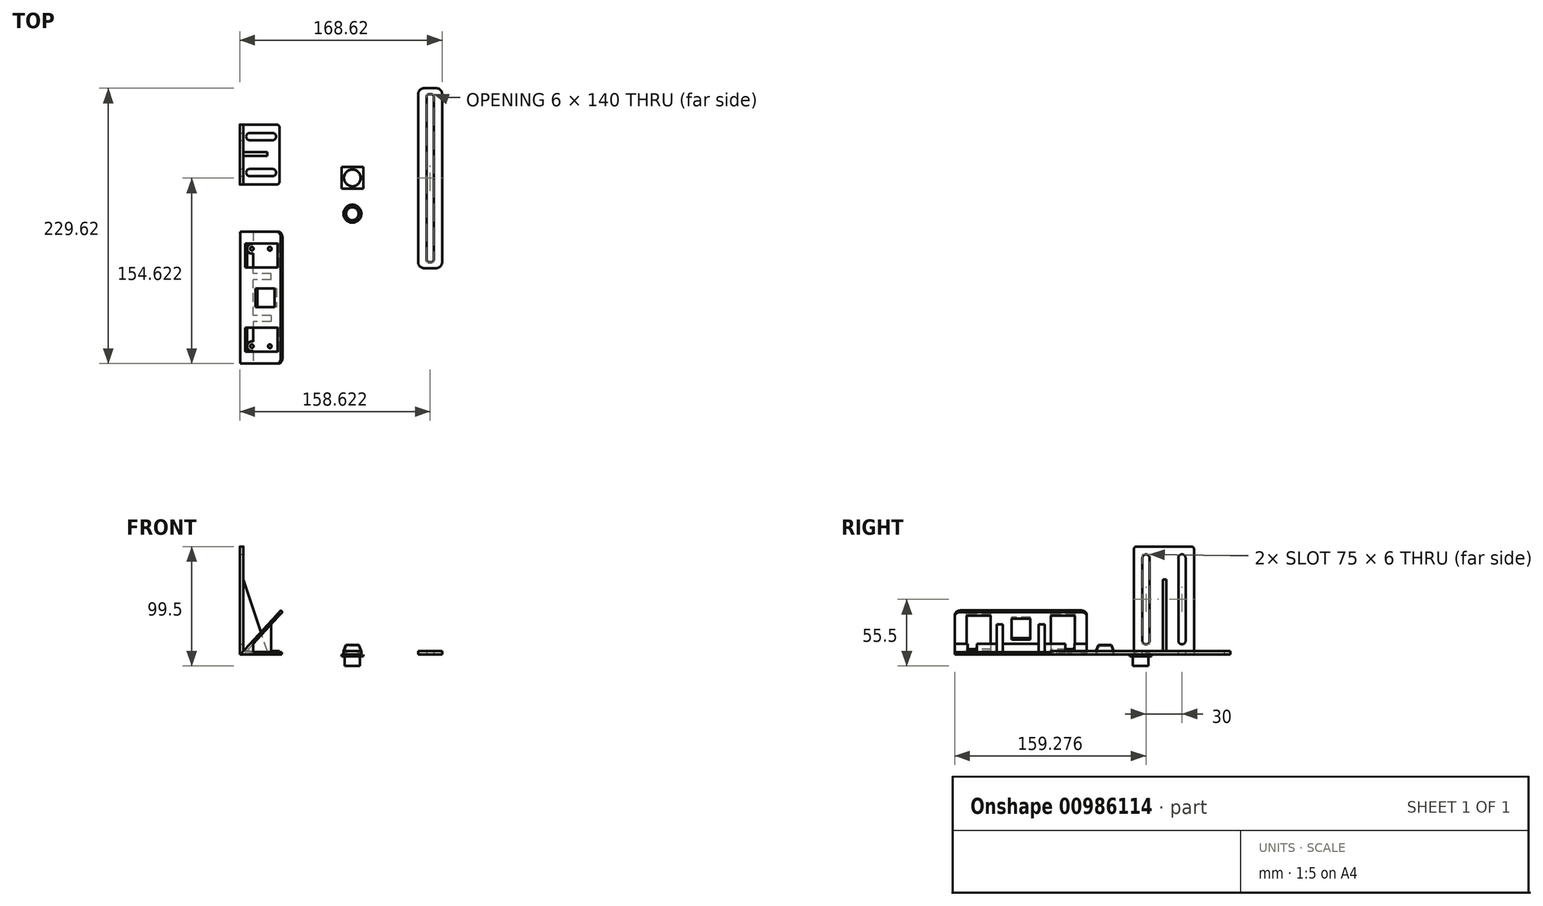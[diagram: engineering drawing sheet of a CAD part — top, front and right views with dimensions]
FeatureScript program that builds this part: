
annotation { "Feature Type Name" : "Feature", "Feature Type Description" : "" }
export const myFeature = defineFeature(function(context is Context, id is Id, definition is map)
    precondition{}
    {
        {
            var Q0;
            Q0=qCreatedBy(makeId("Top.planeOp"),FACE);
            var sketch = newSketch(context, id + "F0", { "sketchPlane" : qUnion([Q0])});
            skCircle(sketch, "E0", {"center": v(0, 0) * mm, "radius": 7 * mm});
            skSolve(sketch);
        }
        {
            var Q0;
            Q0=makeQuery(id+"F0.imprint","IMPRINT",FACE,{"disambiguationData":[TD([[makeQuery(id+"F0.imprint","IMPRINT",EDGE,{"derivedFrom":sQuery(id+"F0.wireOp",EDGE,"E0")}),1.0]])]});
            extrude(context, id + "F1", {"entities" : qUnion([Q0]), "depth" : 2.5 * mm, "offsetDistance" : 25 * mm});
        }
        {
            var Q0;
            Q0=makeQuery(id+"F1.opExtrude","CAP_EDGE",EDGE,{"disambiguationData":[OSD([sQuery(id+"F0.wireOp",EDGE,"E0")])],"isStart":false});
            fillet(context, id + "F2", {"entities" : qUnion([Q0]), "radius" : 7 * mm, "tangentPropagation" : true, "allowEdgeOverflow" : false});
        }
        {
            var Q0;
            Q0=makeQuery(id+"F1.opExtrude","CAP_FACE",FACE,{"disambiguationData":[OSD([sQuery(id+"F0.wireOp",EDGE,"E0")])],"isStart":true});
            cPlane(context, id + "F3", {"entities" : qUnion([Q0]), "cplaneType" : CPlaneType.OFFSET, "offset" : 0 * mm, "width" : 150 * mm, "height" : 150 * mm});
        }
        {
            var Q0;
            Q0=qCreatedBy(id+"F3.planeOp",FACE);
            var sketch = newSketch(context, id + "F4", { "sketchPlane" : qUnion([Q0])});
            skLineSegment(sketch, "E1.bottom", {"start": v(-9, -9) * mm, "end": v(9, -9) * mm});
            skLineSegment(sketch, "E1.top", {"start": v(-9, 9) * mm, "end": v(9, 9) * mm});
            skLineSegment(sketch, "E1.left", {"start": v(-9, -9) * mm, "end": v(-9, 9) * mm});
            skLineSegment(sketch, "E1.right", {"start": v(9, -9) * mm, "end": v(9, 9) * mm});
            skSolve(sketch);
        }
        {
            var Q0;
            Q0=qSketchRegion(id+"F4",true);
            extrude(context, id + "F5", {"entities" : qUnion([Q0]), "operationType" : NewBodyOperationType.ADD, "depth" : 1.5 * mm, "offsetDistance" : 25 * mm});
        }
        {
            var Q0;
            Q0=makeQuery(id+"F5.opExtrude","CAP_FACE",FACE,{"disambiguationData":[OSD([sQuery(id+"F4.wireOp",EDGE,"E1.bottom"),sQuery(id+"F4.wireOp",EDGE,"E1.top"),sQuery(id+"F4.wireOp",EDGE,"E1.left"),sQuery(id+"F4.wireOp",EDGE,"E1.right")])],"isStart":false});
            cPlane(context, id + "F6", {"entities" : qUnion([Q0]), "cplaneType" : CPlaneType.OFFSET, "offset" : 0 * mm, "width" : 150 * mm, "height" : 150 * mm});
        }
        {
            var Q0;
            Q0=qCreatedBy(id+"F6.planeOp",FACE);
            var sketch = newSketch(context, id + "F7", { "sketchPlane" : qUnion([Q0])});
            skCircle(sketch, "E2", {"center": v(0, 0) * mm, "radius": 6.4 * mm});
            skSolve(sketch);
        }
        {
            var Q0;
            Q0=qSketchRegion(id+"F7",true);
            extrude(context, id + "F8", {"entities" : qUnion([Q0]), "operationType" : NewBodyOperationType.ADD, "depth" : 8 * mm, "offsetDistance" : 25 * mm});
        }
        {
            var Q0;
            Q0=qCreatedBy(makeId("Top.planeOp"),FACE);
            var sketch = newSketch(context, id + "F9", { "sketchPlane" : qUnion([Q0])});
            skCircle(sketch, "E3", {"center": v(0, -29.84) * mm, "radius": 7.45 * mm});
            skSolve(sketch);
        }
        {
            var Q0;
            Q0=qSketchRegion(id+"F9",true);
            extrude(context, id + "F10", {"entities" : qUnion([Q0]), "depth" : 8 * mm, "offsetDistance" : 25 * mm});
        }
        {
            var Q0;
            Q0=makeQuery(id+"F10.opExtrude","CAP_EDGE",EDGE,{"disambiguationData":[OSD([sQuery(id+"F9.wireOp",EDGE,"E3")])],"isStart":false});
            chamfer(context, id + "F11", {"entities" : qUnion([Q0]), "chamferType" : ChamferType.TWO_OFFSETS, "width1" : 2 * mm, "oppositeDirection" : false, "width2" : 5 * mm, "tangentPropagation" : true});
        }
        {
            var Q0;
            Q0=qCreatedBy(makeId("Top.planeOp"),FACE);
            var sketch = newSketch(context, id + "F12", { "sketchPlane" : qUnion([Q0])});
            skCircle(sketch, "E4", {"center": v(0, -29.84) * mm, "radius": 6.45 * mm});
            skSolve(sketch);
        }
        {
            var Q0;
            Q0=qSketchRegion(id+"F12",true);
            extrude(context, id + "F13", {"entities" : qUnion([Q0]), "depth" : 7 * mm, "offsetDistance" : 25 * mm});
        }
        {
            var Q0;
            Q0=makeQuery(id+"F13.opExtrude","CAP_EDGE",EDGE,{"disambiguationData":[OSD([sQuery(id+"F12.wireOp",EDGE,"E4")])],"isStart":false});
            chamfer(context, id + "F14", {"entities" : qUnion([Q0]), "chamferType" : ChamferType.TWO_OFFSETS, "width1" : 1.7 * mm, "oppositeDirection" : false, "width2" : 4 * mm, "tangentPropagation" : true});
        }
        {
            var Q0;
            Q0=makeQuery(id+"F13.opExtrude","SWEPT_BODY",BODY,{"disambiguationData":[OSD([sQuery(id+"F12.wireOp",EDGE,"E4")])]});
            var Q1;
            Q1=makeQuery(id+"F10.opExtrude","SWEPT_BODY",BODY,{"disambiguationData":[OSD([sQuery(id+"F9.wireOp",EDGE,"E3")])]});
            booleanBodies(context, id + "F15", {"operationType" : BooleanOperationType.SUBTRACTION, "tools" : qUnion([Q0]), "targets" : qUnion([Q1])});
        }
        {
            var Q0;
            Q0=qCreatedBy(makeId("Top.planeOp"),FACE);
            var sketch = newSketch(context, id + "F16", { "sketchPlane" : qUnion([Q0])});
            skLineSegment(sketch, "E5.bottom", {"start": v(59.8, 74.78) * mm, "end": v(69.8, 74.78) * mm});
            skLineSegment(sketch, "E5.top", {"start": v(59.8, -75.22) * mm, "end": v(69.8, -75.22) * mm});
            skLineSegment(sketch, "E5.left", {"start": v(54.8, 69.78) * mm, "end": v(54.8, -70.22) * mm});
            skLineSegment(sketch, "E5.right", {"start": v(74.8, 69.78) * mm, "end": v(74.8, -70.22) * mm});
            skPoint(sketch, "E6.visualSharp", {"position": v(54.8, 74.78) * mm});
            skArc(sketch, "E6.filletArc", {"start": v(59.8, 74.78) * mm, "mid": v(56.27, 73.32) * mm, "end": v(54.8, 69.78) * mm});
            skPoint(sketch, "E7.visualSharp", {"position": v(74.8, 74.78) * mm});
            skArc(sketch, "E7.filletArc", {"start": v(74.8, 69.78) * mm, "mid": v(73.34, 73.32) * mm, "end": v(69.8, 74.78) * mm});
            skPoint(sketch, "E8.visualSharp", {"position": v(54.8, -75.22) * mm});
            skArc(sketch, "E8.filletArc", {"start": v(54.8, -70.22) * mm, "mid": v(56.27, -73.75) * mm, "end": v(59.8, -75.22) * mm});
            skPoint(sketch, "E9.visualSharp", {"position": v(74.8, -75.22) * mm});
            skArc(sketch, "E9.filletArc", {"start": v(69.8, -75.22) * mm, "mid": v(73.34, -73.75) * mm, "end": v(74.8, -70.22) * mm});
            skLineSegment(sketch, "E10.bottom", {"start": v(63.8, 69.78) * mm, "end": v(65.8, 69.78) * mm});
            skLineSegment(sketch, "E10.top", {"start": v(63.8, -70.22) * mm, "end": v(65.8, -70.22) * mm});
            skLineSegment(sketch, "E10.left", {"start": v(61.8, 67.78) * mm, "end": v(61.8, -68.22) * mm});
            skLineSegment(sketch, "E10.right", {"start": v(67.8, 67.78) * mm, "end": v(67.8, -68.22) * mm});
            skPoint(sketch, "E11.visualSharp", {"position": v(61.8, 69.78) * mm});
            skArc(sketch, "E11.filletArc", {"start": v(63.8, 69.78) * mm, "mid": v(62.39, 69.2) * mm, "end": v(61.8, 67.78) * mm});
            skPoint(sketch, "E12.visualSharp", {"position": v(61.8, -70.22) * mm});
            skArc(sketch, "E12.filletArc", {"start": v(61.8, -68.22) * mm, "mid": v(62.39, -69.63) * mm, "end": v(63.8, -70.22) * mm});
            skPoint(sketch, "E13.visualSharp", {"position": v(67.8, -70.22) * mm});
            skArc(sketch, "E13.filletArc", {"start": v(65.8, -70.22) * mm, "mid": v(67.22, -69.63) * mm, "end": v(67.8, -68.22) * mm});
            skPoint(sketch, "E14.visualSharp", {"position": v(67.8, 69.78) * mm});
            skArc(sketch, "E14.filletArc", {"start": v(67.8, 67.78) * mm, "mid": v(67.22, 69.2) * mm, "end": v(65.8, 69.78) * mm});
            skSolve(sketch);
        }
        {
            var Q0;
            Q0=qSketchRegion(id+"F16",true);
            extrude(context, id + "F17", {"entities" : qUnion([Q0]), "depth" : 3 * mm, "offsetDistance" : 25 * mm});
        }
        {
            var Q0;
            Q0=qCreatedBy(makeId("Top.planeOp"),FACE);
            var sketch = newSketch(context, id + "F18", { "sketchPlane" : qUnion([Q0])});
            skLineSegment(sketch, "E15.bottom", {"start": v(-90.82, 44.44) * mm, "end": v(-62.82, 44.44) * mm});
            skLineSegment(sketch, "E15.top", {"start": v(-90.82, -5.56) * mm, "end": v(-62.82, -5.56) * mm});
            skLineSegment(sketch, "E15.left", {"start": v(-90.82, 44.44) * mm, "end": v(-90.82, -5.56) * mm});
            skLineSegment(sketch, "E15.right", {"start": v(-60.82, 42.44) * mm, "end": v(-60.82, -3.56) * mm});
            skPoint(sketch, "E16.visualSharp", {"position": v(-60.82, 44.44) * mm});
            skArc(sketch, "E16.filletArc", {"start": v(-60.82, 42.44) * mm, "mid": v(-61.4, 43.85) * mm, "end": v(-62.82, 44.44) * mm});
            skPoint(sketch, "E17.visualSharp", {"position": v(-60.82, -5.56) * mm});
            skArc(sketch, "E17.filletArc", {"start": v(-62.82, -5.56) * mm, "mid": v(-61.4, -4.98) * mm, "end": v(-60.82, -3.56) * mm});
            skLineSegment(sketch, "E18.bottom", {"start": v(-101.44, 55.6) * mm, "end": v(-90.82, 55.6) * mm, "construction": true});
            skLineSegment(sketch, "E18.top", {"start": v(-101.44, -19.09) * mm, "end": v(-90.82, -19.09) * mm, "construction": true});
            skLineSegment(sketch, "E18.left", {"start": v(-101.44, 55.6) * mm, "end": v(-101.44, -19.09) * mm, "construction": true});
            skLineSegment(sketch, "E18.right", {"start": v(-90.82, 55.6) * mm, "end": v(-90.82, -19.09) * mm, "construction": true});
            skSolve(sketch);
        }
        {
            var Q0;
            Q0=qSketchRegion(id+"F18",true);
            extrude(context, id + "F19", {"entities" : qUnion([Q0]), "depth" : 3 * mm, "offsetDistance" : 25 * mm});
        }
        {
            var Q0;
            Q0=qCreatedBy(makeId("Top.planeOp"),FACE);
            var sketch = newSketch(context, id + "F20", { "sketchPlane" : qUnion([Q0])});
            skLineSegment(sketch, "E19.bottom", {"start": v(-93.82, 44.44) * mm, "end": v(-90.82, 44.44) * mm});
            skLineSegment(sketch, "E19.top", {"start": v(-93.82, -5.56) * mm, "end": v(-90.82, -5.56) * mm});
            skLineSegment(sketch, "E19.left", {"start": v(-93.82, 44.44) * mm, "end": v(-93.82, -5.56) * mm});
            skLineSegment(sketch, "E19.right", {"start": v(-90.82, 44.44) * mm, "end": v(-90.82, -5.56) * mm});
            skSolve(sketch);
        }
        {
            var Q0;
            Q0=qSketchRegion(id+"F20",true);
            extrude(context, id + "F21", {"entities" : qUnion([Q0]), "operationType" : NewBodyOperationType.ADD, "depth" : 90 * mm, "offsetDistance" : 25 * mm});
        }
        {
            var Q0;
            Q0=makeQuery(id+"F21.opExtrude","CAP_EDGE",EDGE,{"disambiguationData":[OSD([sQuery(id+"F20.wireOp",EDGE,"E19.top")])],"isStart":false});
            var Q1;
            Q1=makeQuery(id+"F21.opExtrude","CAP_EDGE",EDGE,{"disambiguationData":[OSD([sQuery(id+"F20.wireOp",EDGE,"E19.bottom")])],"isStart":false});
            fillet(context, id + "F22", {"entities" : qUnion([Q0, Q1]), "radius" : 2 * mm, "tangentPropagation" : true, "allowEdgeOverflow" : false});
        }
        {
            var Q0;
            Q0=makeQuery(id+"F19.opExtrude","CAP_FACE",FACE,{"disambiguationData":[OSD([sQuery(id+"F18.wireOp",EDGE,"E15.bottom"),sQuery(id+"F18.wireOp",EDGE,"E15.top"),sQuery(id+"F18.wireOp",EDGE,"E15.left"),sQuery(id+"F18.wireOp",EDGE,"E15.right"),sQuery(id+"F18.wireOp",EDGE,"E16.filletArc"),sQuery(id+"F18.wireOp",EDGE,"E17.filletArc")])],"isStart":false});
            var sketch = newSketch(context, id + "F23", { "sketchPlane" : qUnion([Q0])});
            skLineSegment(sketch, "E20.bottom", {"start": v(-85.49, 37.44) * mm, "end": v(-66.49, 37.44) * mm});
            skLineSegment(sketch, "E20.top", {"start": v(-85.49, 31.44) * mm, "end": v(-66.49, 31.44) * mm});
            skLineSegment(sketch, "E20.left", {"start": v(-88.49, 34.44) * mm, "end": v(-88.49, 34.44) * mm});
            skLineSegment(sketch, "E20.right", {"start": v(-63.49, 34.44) * mm, "end": v(-63.49, 34.44) * mm});
            skPoint(sketch, "E21.visualSharp", {"position": v(-88.49, 37.44) * mm});
            skArc(sketch, "E21.filletArc", {"start": v(-85.49, 37.44) * mm, "mid": v(-87.6, 36.56) * mm, "end": v(-88.49, 34.44) * mm});
            skPoint(sketch, "E22.visualSharp", {"position": v(-88.49, 31.44) * mm});
            skArc(sketch, "E22.filletArc", {"start": v(-88.49, 34.44) * mm, "mid": v(-87.6, 32.31) * mm, "end": v(-85.49, 31.44) * mm});
            skPoint(sketch, "E23.visualSharp", {"position": v(-63.49, 31.44) * mm});
            skArc(sketch, "E23.filletArc", {"start": v(-66.49, 31.44) * mm, "mid": v(-64.37, 32.31) * mm, "end": v(-63.49, 34.44) * mm});
            skPoint(sketch, "E24.visualSharp", {"position": v(-63.49, 37.44) * mm});
            skArc(sketch, "E24.filletArc", {"start": v(-63.49, 34.44) * mm, "mid": v(-64.37, 36.56) * mm, "end": v(-66.49, 37.44) * mm});
            skLineSegment(sketch, "E25.bottom", {"start": v(-85.49, 7.44) * mm, "end": v(-66.49, 7.44) * mm});
            skLineSegment(sketch, "E25.top", {"start": v(-85.49, 1.44) * mm, "end": v(-66.49, 1.44) * mm});
            skLineSegment(sketch, "E25.left", {"start": v(-88.49, 4.44) * mm, "end": v(-88.49, 4.44) * mm});
            skLineSegment(sketch, "E25.right", {"start": v(-63.49, 4.44) * mm, "end": v(-63.49, 4.44) * mm});
            skPoint(sketch, "E26.visualSharp", {"position": v(-88.49, 7.44) * mm});
            skArc(sketch, "E26.filletArc", {"start": v(-85.49, 7.44) * mm, "mid": v(-87.61, 6.56) * mm, "end": v(-88.49, 4.44) * mm});
            skPoint(sketch, "E27.visualSharp", {"position": v(-88.49, 1.44) * mm});
            skArc(sketch, "E27.filletArc", {"start": v(-88.49, 4.44) * mm, "mid": v(-87.61, 2.31) * mm, "end": v(-85.49, 1.44) * mm});
            skPoint(sketch, "E28.visualSharp", {"position": v(-63.49, 1.44) * mm});
            skArc(sketch, "E28.filletArc", {"start": v(-66.49, 1.44) * mm, "mid": v(-64.37, 2.31) * mm, "end": v(-63.49, 4.44) * mm});
            skPoint(sketch, "E29.visualSharp", {"position": v(-63.49, 7.44) * mm});
            skArc(sketch, "E29.filletArc", {"start": v(-63.49, 4.44) * mm, "mid": v(-64.37, 6.56) * mm, "end": v(-66.49, 7.44) * mm});
            skSolve(sketch);
        }
        {
            var Q0;
            Q0=qSketchRegion(id+"F23",true);
            extrude(context, id + "F24", {"entities" : qUnion([Q0]), "operationType" : NewBodyOperationType.REMOVE, "oppositeDirection" : true, "depth" : 25 * mm, "offsetDistance" : 25 * mm});
        }
        {
            var Q0;
            Q0=makeQuery(id+"F21.opExtrude","SWEPT_FACE",FACE,{"disambiguationData":[OSD([sQuery(id+"F20.wireOp",EDGE,"E19.right")])]});
            var sketch = newSketch(context, id + "F25", { "sketchPlane" : qUnion([Q0])});
            skLineSegment(sketch, "E30.bottom", {"start": v(34.44, 83.5) * mm, "end": v(34.44, 83.5) * mm});
            skLineSegment(sketch, "E30.top", {"start": v(34.44, 8.5) * mm, "end": v(34.44, 8.5) * mm});
            skLineSegment(sketch, "E30.left", {"start": v(31.44, 80.5) * mm, "end": v(31.44, 11.5) * mm});
            skLineSegment(sketch, "E30.right", {"start": v(37.44, 80.5) * mm, "end": v(37.44, 11.5) * mm});
            skPoint(sketch, "E31.visualSharp", {"position": v(31.44, 83.5) * mm});
            skArc(sketch, "E31.filletArc", {"start": v(34.44, 83.5) * mm, "mid": v(32.31, 82.62) * mm, "end": v(31.44, 80.5) * mm});
            skPoint(sketch, "E32.visualSharp", {"position": v(31.44, 8.5) * mm});
            skArc(sketch, "E32.filletArc", {"start": v(31.44, 11.5) * mm, "mid": v(32.31, 9.38) * mm, "end": v(34.44, 8.5) * mm});
            skPoint(sketch, "E33.visualSharp", {"position": v(37.44, 83.5) * mm});
            skArc(sketch, "E33.filletArc", {"start": v(37.44, 80.5) * mm, "mid": v(36.56, 82.62) * mm, "end": v(34.44, 83.5) * mm});
            skPoint(sketch, "E34.visualSharp", {"position": v(37.44, 8.5) * mm});
            skArc(sketch, "E34.filletArc", {"start": v(34.44, 8.5) * mm, "mid": v(36.56, 9.38) * mm, "end": v(37.44, 11.5) * mm});
            skLineSegment(sketch, "E35.bottom", {"start": v(49.07, 61.34) * mm, "end": v(49.07, 61.34) * mm});
            skLineSegment(sketch, "E35.top", {"start": v(49.07, -13.66) * mm, "end": v(49.07, -13.66) * mm});
            skLineSegment(sketch, "E35.left", {"start": v(1.44, 80.5) * mm, "end": v(1.44, 11.5) * mm});
            skLineSegment(sketch, "E35.right", {"start": v(7.44, 80.5) * mm, "end": v(7.44, 11.5) * mm});
            skPoint(sketch, "E36.visualSharp", {"position": v(1.44, 83.5) * mm});
            skArc(sketch, "E36.filletArc", {"start": v(4.44, 83.5) * mm, "mid": v(2.31, 82.62) * mm, "end": v(1.44, 80.5) * mm});
            skPoint(sketch, "E37.visualSharp", {"position": v(1.44, 8.5) * mm});
            skArc(sketch, "E37.filletArc", {"start": v(1.44, 11.5) * mm, "mid": v(2.31, 9.38) * mm, "end": v(4.44, 8.5) * mm});
            skPoint(sketch, "E38.visualSharp", {"position": v(7.44, 83.5) * mm});
            skArc(sketch, "E38.filletArc", {"start": v(7.44, 80.5) * mm, "mid": v(6.56, 82.62) * mm, "end": v(4.44, 83.5) * mm});
            skPoint(sketch, "E39.visualSharp", {"position": v(7.44, 8.5) * mm});
            skArc(sketch, "E39.filletArc", {"start": v(4.44, 8.5) * mm, "mid": v(6.56, 9.38) * mm, "end": v(7.44, 11.5) * mm});
            skSolve(sketch);
        }
        {
            var Q0;
            Q0=qSketchRegion(id+"F25",true);
            extrude(context, id + "F26", {"entities" : qUnion([Q0]), "operationType" : NewBodyOperationType.REMOVE, "oppositeDirection" : true, "depth" : 25 * mm, "offsetDistance" : 25 * mm});
        }
        {
            var Q0;
            Q0=makeQuery(id+"F29.boolean.opBoolean","MERGE",FACE,{"derivedFrom":[makeQuery(id+"F21.boolean.opBoolean","MERGE",FACE,{"derivedFrom":[makeQuery(id+"F19.opExtrude","SWEPT_FACE",FACE,{"disambiguationData":[OSD([sQuery(id+"F18.wireOp",EDGE,"E15.top")])]}),makeQuery(id+"F21.opExtrude","SWEPT_FACE",FACE,{"disambiguationData":[OSD([sQuery(id+"F20.wireOp",EDGE,"E19.top")])]})]}),makeQuery(id+"F29.opExtrude","CAP_FACE",FACE,{"disambiguationData":[OSD([sQuery(id+"F28.wireOp",EDGE,"E40"),sQuery(id+"F28.wireOp",EDGE,"E41"),sQuery(id+"F28.wireOp",EDGE,"E42")])],"isStart":true})]});
            cPlane(context, id + "F27", {"entities" : qUnion([Q0]), "cplaneType" : CPlaneType.OFFSET, "offset" : 24 * mm, "oppositeDirection" : true, "width" : 150 * mm, "height" : 150 * mm});
        }
        {
            var Q0;
            Q0=qCreatedBy(id+"F27.planeOp",FACE);
            var sketch = newSketch(context, id + "F28", { "sketchPlane" : qUnion([Q0])});
            skLineSegment(sketch, "E40", {"start": v(-90.82, 62.64) * mm, "end": v(-90.82, 3) * mm});
            skLineSegment(sketch, "E41", {"start": v(-90.82, 3) * mm, "end": v(-70.95, 3) * mm});
            skLineSegment(sketch, "E42", {"start": v(-70.95, 3) * mm, "end": v(-90.82, 62.64) * mm});
            skSolve(sketch);
        }
        {
            var Q0;
            Q0=makeQuery(id+"F28.imprint","IMPRINT",FACE,{"disambiguationData":[TD([[makeQuery(id+"F28.imprint","IMPRINT",EDGE,{"derivedFrom":sQuery(id+"F28.wireOp",EDGE,"E40")}),1.0]])]});
            extrude(context, id + "F29", {"entities" : qUnion([Q0]), "operationType" : NewBodyOperationType.ADD, "oppositeDirection" : true, "depth" : 3 * mm, "offsetDistance" : 25 * mm});
        }
        {
            var Q0;
            Q0=qCreatedBy(makeId("Top.planeOp"),FACE);
            var sketch = newSketch(context, id + "F30", { "sketchPlane" : qUnion([Q0])});
            skLineSegment(sketch, "E43.bottom", {"start": v(-88.77, -44.84) * mm, "end": v(-63.77, -44.84) * mm});
            skLineSegment(sketch, "E43.top", {"start": v(-88.77, -154.84) * mm, "end": v(-63.77, -154.84) * mm});
            skLineSegment(sketch, "E43.left", {"start": v(-88.77, -44.84) * mm, "end": v(-88.77, -154.84) * mm});
            skLineSegment(sketch, "E43.right", {"start": v(-58.77, -49.84) * mm, "end": v(-58.77, -149.84) * mm});
            skPoint(sketch, "E44.visualSharp", {"position": v(-58.77, -44.84) * mm});
            skArc(sketch, "E44.filletArc", {"start": v(-58.77, -49.84) * mm, "mid": v(-60.23, -46.3) * mm, "end": v(-63.77, -44.84) * mm});
            skPoint(sketch, "E45.visualSharp", {"position": v(-58.77, -154.84) * mm});
            skArc(sketch, "E45.filletArc", {"start": v(-63.77, -154.84) * mm, "mid": v(-60.23, -153.38) * mm, "end": v(-58.77, -149.84) * mm});
            skSolve(sketch);
        }
        {
            var Q0;
            Q0=qSketchRegion(id+"F30",true);
            extrude(context, id + "F31", {"entities" : qUnion([Q0]), "depth" : 2 * mm, "offsetDistance" : 25 * mm});
        }
        {
            var Q0;
            Q0=makeQuery(id+"F31.opExtrude","SWEPT_FACE",FACE,{"disambiguationData":[OSD([sQuery(id+"F30.wireOp",EDGE,"E43.top")])]});
            var sketch = newSketch(context, id + "F32", { "sketchPlane" : qUnion([Q0])});
            skLineSegment(sketch, "E46", {"start": v(-88.77, 2) * mm, "end": v(-58.2, 35.45) * mm});
            skLineSegment(sketch, "E47", {"start": v(-58.2, 35.45) * mm, "end": v(-59.67, 36.8) * mm});
            skLineSegment(sketch, "E48", {"start": v(-59.67, 36.8) * mm, "end": v(-93.3, 0) * mm});
            skLineSegment(sketch, "E49", {"start": v(-93.3, 0) * mm, "end": v(-88.77, 0) * mm});
            skLineSegment(sketch, "E50", {"start": v(-88.77, 0) * mm, "end": v(-88.77, 2) * mm});
            skSolve(sketch);
        }
        {
            var Q0;
            Q0=qSketchRegion(id+"F32",true);
            extrude(context, id + "F33", {"entities" : qUnion([Q0]), "operationType" : NewBodyOperationType.ADD, "oppositeDirection" : true, "depth" : 110 * mm, "offsetDistance" : 25 * mm});
        }
        {
            var Q0;
            Q0=makeQuery(id+"F33.opExtrude","CAP_EDGE",EDGE,{"disambiguationData":[OSD([sQuery(id+"F32.wireOp",EDGE,"E47")])],"isStart":true});
            var Q1;
            Q1=makeQuery(id+"F33.opExtrude","CAP_EDGE",EDGE,{"disambiguationData":[OSD([sQuery(id+"F32.wireOp",EDGE,"E47")])],"isStart":false});
            fillet(context, id + "F34", {"entities" : qUnion([Q0, Q1]), "radius" : 5 * mm, "tangentPropagation" : true, "allowEdgeOverflow" : false});
        }
        {
            var Q0;
            Q0=makeQuery(id+"F33.boolean.opBoolean","MERGE",FACE,{"derivedFrom":[makeQuery(id+"F31.opExtrude","SWEPT_FACE",FACE,{"disambiguationData":[OSD([sQuery(id+"F30.wireOp",EDGE,"E43.top")])]}),makeQuery(id+"F33.opExtrude","CAP_FACE",FACE,{"disambiguationData":[OSD([sQuery(id+"F32.wireOp",EDGE,"E46"),sQuery(id+"F32.wireOp",EDGE,"E47"),sQuery(id+"F32.wireOp",EDGE,"E48"),sQuery(id+"F32.wireOp",EDGE,"E49"),sQuery(id+"F32.wireOp",EDGE,"E50")])],"isStart":true})]});
            var sketch = newSketch(context, id + "F35", { "sketchPlane" : qUnion([Q0])});
            skLineSegment(sketch, "E51", {"start": v(-88.77, 2) * mm, "end": v(-82.5, 8.86) * mm});
            skLineSegment(sketch, "E52", {"start": v(-82.5, 8.86) * mm, "end": v(-82.5, 2) * mm});
            skLineSegment(sketch, "E53", {"start": v(-82.5, 2) * mm, "end": v(-88.77, 2) * mm});
            skSolve(sketch);
        }
        {
            var Q0;
            Q0=qSketchRegion(id+"F35",true);
            extrude(context, id + "F36", {"entities" : qUnion([Q0]), "operationType" : NewBodyOperationType.ADD, "oppositeDirection" : true, "depth" : 110 * mm, "offsetDistance" : 25 * mm});
        }
        {
            var Q0;
            Q0=qCreatedBy(makeId("Top.planeOp"),FACE);
            cPlane(context, id + "F37", {"entities" : qUnion([Q0]), "cplaneType" : CPlaneType.OFFSET, "offset" : 50 * mm, "width" : 150 * mm, "height" : 150 * mm});
        }
        {
            var Q0;
            Q0=qCreatedBy(id+"F37.planeOp",FACE);
            var sketch = newSketch(context, id + "F38", { "sketchPlane" : qUnion([Q0])});
            skPoint(sketch, "E54", {"position": v(-68.77, -59.07) * mm});
            skPoint(sketch, "E55", {"position": v(-83.77, -59.07) * mm});
            skPoint(sketch, "E56", {"position": v(-68.77, -140.34) * mm});
            skPoint(sketch, "E57", {"position": v(-83.77, -140.34) * mm});
            skSolve(sketch);
        }
        {
            var Q0;
            Q0=sQuery(id+"F38.wireOp",VERTEX,"E57");
            var Q1;
            Q1=sQuery(id+"F38.wireOp",VERTEX,"E56");
            var Q2;
            Q2=sQuery(id+"F38.wireOp",VERTEX,"E55");
            var Q3;
            Q3=sQuery(id+"F38.wireOp",VERTEX,"E54");
            var Q4;
            Q4=makeQuery(id+"F31.opExtrude","SWEPT_BODY",BODY,{"disambiguationData":[OSD([sQuery(id+"F30.wireOp",EDGE,"E43.bottom"),sQuery(id+"F30.wireOp",EDGE,"E43.top"),sQuery(id+"F30.wireOp",EDGE,"E43.left"),sQuery(id+"F30.wireOp",EDGE,"E43.right"),sQuery(id+"F30.wireOp",EDGE,"E44.filletArc"),sQuery(id+"F30.wireOp",EDGE,"E45.filletArc")])]});
            hole(context, id + "F39", {"style" : HoleStyle.SIMPLE, "endStyle" : HoleEndStyle.BLIND, "holeDiameter" : 3 * mm, "holeDepth" : 50 * mm, "tappedDepth" : 12 * mm, "tapClearance" : 3, "locations" : qUnion([Q0, Q1, Q2, Q3]), "scope" : qUnion([Q4])});
        }
        {
            var Q0;
            Q0=qCreatedBy(id+"F37.planeOp",FACE);
            var sketch = newSketch(context, id + "F40", { "sketchPlane" : qUnion([Q0])});
            skPoint(sketch, "E58", {"position": v(-68.77, -59.07) * mm});
            skPoint(sketch, "E59", {"position": v(-83.77, -59.07) * mm});
            skPoint(sketch, "E60", {"position": v(-68.77, -140.34) * mm});
            skPoint(sketch, "E61", {"position": v(-83.77, -140.34) * mm});
            skSolve(sketch);
        }
        {
            var Q0;
            Q0=sQuery(id+"F40.wireOp",VERTEX,"E61");
            var Q1;
            Q1=sQuery(id+"F40.wireOp",VERTEX,"E60");
            var Q2;
            Q2=sQuery(id+"F40.wireOp",VERTEX,"E58");
            var Q3;
            Q3=sQuery(id+"F40.wireOp",VERTEX,"E59");
            var Q4;
            Q4=makeQuery(id+"F31.opExtrude","SWEPT_BODY",BODY,{"disambiguationData":[OSD([sQuery(id+"F30.wireOp",EDGE,"E43.bottom"),sQuery(id+"F30.wireOp",EDGE,"E43.top"),sQuery(id+"F30.wireOp",EDGE,"E43.left"),sQuery(id+"F30.wireOp",EDGE,"E43.right"),sQuery(id+"F30.wireOp",EDGE,"E44.filletArc"),sQuery(id+"F30.wireOp",EDGE,"E45.filletArc")])]});
            hole(context, id + "F41", {"style" : HoleStyle.SIMPLE, "endStyle" : HoleEndStyle.BLIND, "holeDiameter" : 8 * mm, "holeDepth" : 19 * mm, "tappedDepth" : 12 * mm, "tapClearance" : 3, "locations" : qUnion([Q0, Q1, Q2, Q3]), "scope" : qUnion([Q4])});
        }
        {
            var Q0;
            Q0=makeQuery(id+"F33.boolean.opBoolean","MERGE",FACE,{"derivedFrom":[makeQuery(id+"F31.opExtrude","CAP_FACE",FACE,{"disambiguationData":[OSD([sQuery(id+"F30.wireOp",EDGE,"E43.bottom"),sQuery(id+"F30.wireOp",EDGE,"E43.top"),sQuery(id+"F30.wireOp",EDGE,"E43.left"),sQuery(id+"F30.wireOp",EDGE,"E43.right"),sQuery(id+"F30.wireOp",EDGE,"E44.filletArc"),sQuery(id+"F30.wireOp",EDGE,"E45.filletArc")])],"isStart":true}),makeQuery(id+"F33.opExtrude","SWEPT_FACE",FACE,{"disambiguationData":[OSD([sQuery(id+"F32.wireOp",EDGE,"E49")])]})]});
            var sketch = newSketch(context, id + "F42", { "sketchPlane" : qUnion([Q0])});
            skCircle(sketch, "E62", {"center": v(-83.77, 59.07) * mm, "radius": 4 * mm});
            skCircle(sketch, "E63", {"center": v(-83.77, 140.34) * mm, "radius": 4 * mm});
            skSolve(sketch);
        }
        {
            var Q0;
            Q0=qSketchRegion(id+"F42",true);
            extrude(context, id + "F43", {"entities" : qUnion([Q0]), "operationType" : NewBodyOperationType.ADD, "oppositeDirection" : true, "depth" : 2 * mm, "offsetDistance" : 25 * mm});
        }
        {
            var Q0;
            Q0=makeQuery(id+"F43.boolean.opBoolean","MERGE",FACE,{"derivedFrom":[makeQuery(id+"F31.opExtrude","CAP_FACE",FACE,{"disambiguationData":[OSD([sQuery(id+"F30.wireOp",EDGE,"E43.bottom"),sQuery(id+"F30.wireOp",EDGE,"E43.top"),sQuery(id+"F30.wireOp",EDGE,"E43.left"),sQuery(id+"F30.wireOp",EDGE,"E43.right"),sQuery(id+"F30.wireOp",EDGE,"E44.filletArc"),sQuery(id+"F30.wireOp",EDGE,"E45.filletArc")])],"isStart":false}),makeQuery(id+"F43.opExtrude","CAP_FACE",FACE,{"disambiguationData":[OSD([sQuery(id+"F42.wireOp",EDGE,"E62")])],"isStart":false}),makeQuery(id+"F43.opExtrude","CAP_FACE",FACE,{"disambiguationData":[OSD([sQuery(id+"F42.wireOp",EDGE,"E63")])],"isStart":false})]});
            var sketch = newSketch(context, id + "F44", { "sketchPlane" : qUnion([Q0])});
            skPoint(sketch, "E64", {"position": v(-83.77, -59.07) * mm});
            skPoint(sketch, "E65", {"position": v(-83.77, -140.34) * mm});
            skSolve(sketch);
        }
        {
            var Q0;
            Q0=sQuery(id+"F44.wireOp",VERTEX,"E64");
            var Q1;
            Q1=sQuery(id+"F44.wireOp",VERTEX,"E65");
            var Q2;
            Q2=makeQuery(id+"F31.opExtrude","SWEPT_BODY",BODY,{"disambiguationData":[OSD([sQuery(id+"F30.wireOp",EDGE,"E43.bottom"),sQuery(id+"F30.wireOp",EDGE,"E43.top"),sQuery(id+"F30.wireOp",EDGE,"E43.left"),sQuery(id+"F30.wireOp",EDGE,"E43.right"),sQuery(id+"F30.wireOp",EDGE,"E44.filletArc"),sQuery(id+"F30.wireOp",EDGE,"E45.filletArc")])]});
            hole(context, id + "F45", {"style" : HoleStyle.SIMPLE, "endStyle" : HoleEndStyle.BLIND, "holeDiameter" : 3 * mm, "holeDepth" : 19 * mm, "tappedDepth" : 12 * mm, "tapClearance" : 3, "locations" : qUnion([Q0, Q1]), "scope" : qUnion([Q2])});
        }
        {
            var Q0;
            Q0=makeQuery(id+"F33.opExtrude","SWEPT_FACE",FACE,{"disambiguationData":[OSD([sQuery(id+"F32.wireOp",EDGE,"E48")])]});
            cPlane(context, id + "F46", {"entities" : qUnion([Q0]), "cplaneType" : CPlaneType.OFFSET, "offset" : 25 * mm, "width" : 150 * mm, "height" : 150 * mm});
        }
        {
            var Q0;
            Q0=qCreatedBy(id+"F46.planeOp",FACE);
            var sketch = newSketch(context, id + "F47", { "sketchPlane" : qUnion([Q0])});
            skLineSegment(sketch, "E66.bottom", {"start": v(54.84, -16.95) * mm, "end": v(74.84, -16.95) * mm});
            skLineSegment(sketch, "E66.top", {"start": v(54.84, -56.95) * mm, "end": v(74.84, -56.95) * mm});
            skLineSegment(sketch, "E66.left", {"start": v(54.84, -16.95) * mm, "end": v(54.84, -56.95) * mm});
            skLineSegment(sketch, "E66.right", {"start": v(74.84, -16.95) * mm, "end": v(74.84, -56.95) * mm});
            skLineSegment(sketch, "E67.bottom", {"start": v(124.84, -16.95) * mm, "end": v(144.84, -16.95) * mm});
            skLineSegment(sketch, "E67.top", {"start": v(124.84, -56.95) * mm, "end": v(144.84, -56.95) * mm});
            skLineSegment(sketch, "E67.left", {"start": v(124.84, -16.95) * mm, "end": v(124.84, -56.95) * mm});
            skLineSegment(sketch, "E67.right", {"start": v(144.84, -16.95) * mm, "end": v(144.84, -56.95) * mm});
            skLineSegment(sketch, "E68.bottom", {"start": v(92.04, -20.68) * mm, "end": v(107.66, -20.68) * mm});
            skLineSegment(sketch, "E68.top", {"start": v(92.04, -44.21) * mm, "end": v(107.66, -44.21) * mm});
            skLineSegment(sketch, "E68.left", {"start": v(92.04, -20.68) * mm, "end": v(92.04, -44.21) * mm});
            skLineSegment(sketch, "E68.right", {"start": v(107.66, -20.68) * mm, "end": v(107.66, -44.21) * mm});
            skSolve(sketch);
        }
        {
            var Q0;
            Q0=qSketchRegion(id+"F47",true);
            extrude(context, id + "F48", {"entities" : qUnion([Q0]), "operationType" : NewBodyOperationType.REMOVE, "oppositeDirection" : true, "depth" : 27 * mm, "offsetDistance" : 25 * mm});
        }
        {
            var Q0;
            Q0=makeQuery(id+"F36.boolean.opBoolean","MERGE",FACE,{"derivedFrom":[makeQuery(id+"F33.boolean.opBoolean","MERGE",FACE,{"derivedFrom":[makeQuery(id+"F31.opExtrude","SWEPT_FACE",FACE,{"disambiguationData":[OSD([sQuery(id+"F30.wireOp",EDGE,"E43.top")])]}),makeQuery(id+"F33.opExtrude","CAP_FACE",FACE,{"disambiguationData":[OSD([sQuery(id+"F32.wireOp",EDGE,"E46"),sQuery(id+"F32.wireOp",EDGE,"E47"),sQuery(id+"F32.wireOp",EDGE,"E48"),sQuery(id+"F32.wireOp",EDGE,"E49"),sQuery(id+"F32.wireOp",EDGE,"E50")])],"isStart":true})]}),makeQuery(id+"F36.opExtrude","CAP_FACE",FACE,{"disambiguationData":[OSD([sQuery(id+"F35.wireOp",EDGE,"E51"),sQuery(id+"F35.wireOp",EDGE,"E52"),sQuery(id+"F35.wireOp",EDGE,"E53")])],"isStart":true})]});
            cPlane(context, id + "F49", {"entities" : qUnion([Q0]), "cplaneType" : CPlaneType.OFFSET, "offset" : 35 * mm, "oppositeDirection" : true, "width" : 150 * mm, "height" : 150 * mm});
        }
        {
            var Q0;
            Q0=makeQuery(id+"F36.boolean.opBoolean","MERGE",FACE,{"derivedFrom":[makeQuery(id+"F33.boolean.opBoolean","MERGE",FACE,{"derivedFrom":[makeQuery(id+"F31.opExtrude","SWEPT_FACE",FACE,{"disambiguationData":[OSD([sQuery(id+"F30.wireOp",EDGE,"E43.bottom")])]}),makeQuery(id+"F33.opExtrude","CAP_FACE",FACE,{"disambiguationData":[OSD([sQuery(id+"F32.wireOp",EDGE,"E46"),sQuery(id+"F32.wireOp",EDGE,"E47"),sQuery(id+"F32.wireOp",EDGE,"E48"),sQuery(id+"F32.wireOp",EDGE,"E49"),sQuery(id+"F32.wireOp",EDGE,"E50")])],"isStart":false})]}),makeQuery(id+"F36.opExtrude","CAP_FACE",FACE,{"disambiguationData":[OSD([sQuery(id+"F35.wireOp",EDGE,"E51"),sQuery(id+"F35.wireOp",EDGE,"E52"),sQuery(id+"F35.wireOp",EDGE,"E53")])],"isStart":false})]});
            cPlane(context, id + "F50", {"entities" : qUnion([Q0]), "cplaneType" : CPlaneType.OFFSET, "offset" : 35 * mm, "oppositeDirection" : true, "width" : 150 * mm, "height" : 150 * mm});
        }
        {
            var Q0;
            Q0=qCreatedBy(id+"F49.planeOp",FACE);
            var sketch = newSketch(context, id + "F51", { "sketchPlane" : qUnion([Q0])});
            skLineSegment(sketch, "E69", {"start": v(-67.67, 2) * mm, "end": v(-82.5, 2) * mm});
            skLineSegment(sketch, "E70", {"start": v(-82.5, 2) * mm, "end": v(-82.5, 8.86) * mm});
            skLineSegment(sketch, "E71", {"start": v(-82.5, 8.86) * mm, "end": v(-67.67, 25.08) * mm});
            skLineSegment(sketch, "E72", {"start": v(-67.67, 25.08) * mm, "end": v(-67.67, 2) * mm});
            skSolve(sketch);
        }
        {
            var Q0;
            Q0=qSketchRegion(id+"F51",true);
            extrude(context, id + "F52", {"entities" : qUnion([Q0]), "operationType" : NewBodyOperationType.ADD, "oppositeDirection" : true, "depth" : 5 * mm, "offsetDistance" : 25 * mm});
        }
        {
            var Q0;
            Q0=qCreatedBy(id+"F50.planeOp",FACE);
            var sketch = newSketch(context, id + "F53", { "sketchPlane" : qUnion([Q0])});
            skLineSegment(sketch, "E73.MirrorCS", {"start": v(67.67, 2) * mm, "end": v(82.5, 2) * mm});
            skLineSegment(sketch, "E74.MirrorCS", {"start": v(82.5, 2) * mm, "end": v(82.5, 8.86) * mm});
            skLineSegment(sketch, "E75.MirrorCS", {"start": v(82.5, 8.86) * mm, "end": v(67.67, 25.08) * mm});
            skLineSegment(sketch, "E76.MirrorCS", {"start": v(67.67, 25.08) * mm, "end": v(67.67, 2) * mm});
            skSolve(sketch);
        }
        {
            var Q0;
            Q0=qSketchRegion(id+"F53",true);
            extrude(context, id + "F54", {"entities" : qUnion([Q0]), "operationType" : NewBodyOperationType.ADD, "oppositeDirection" : true, "depth" : 5 * mm, "offsetDistance" : 25 * mm});
        }
    });
